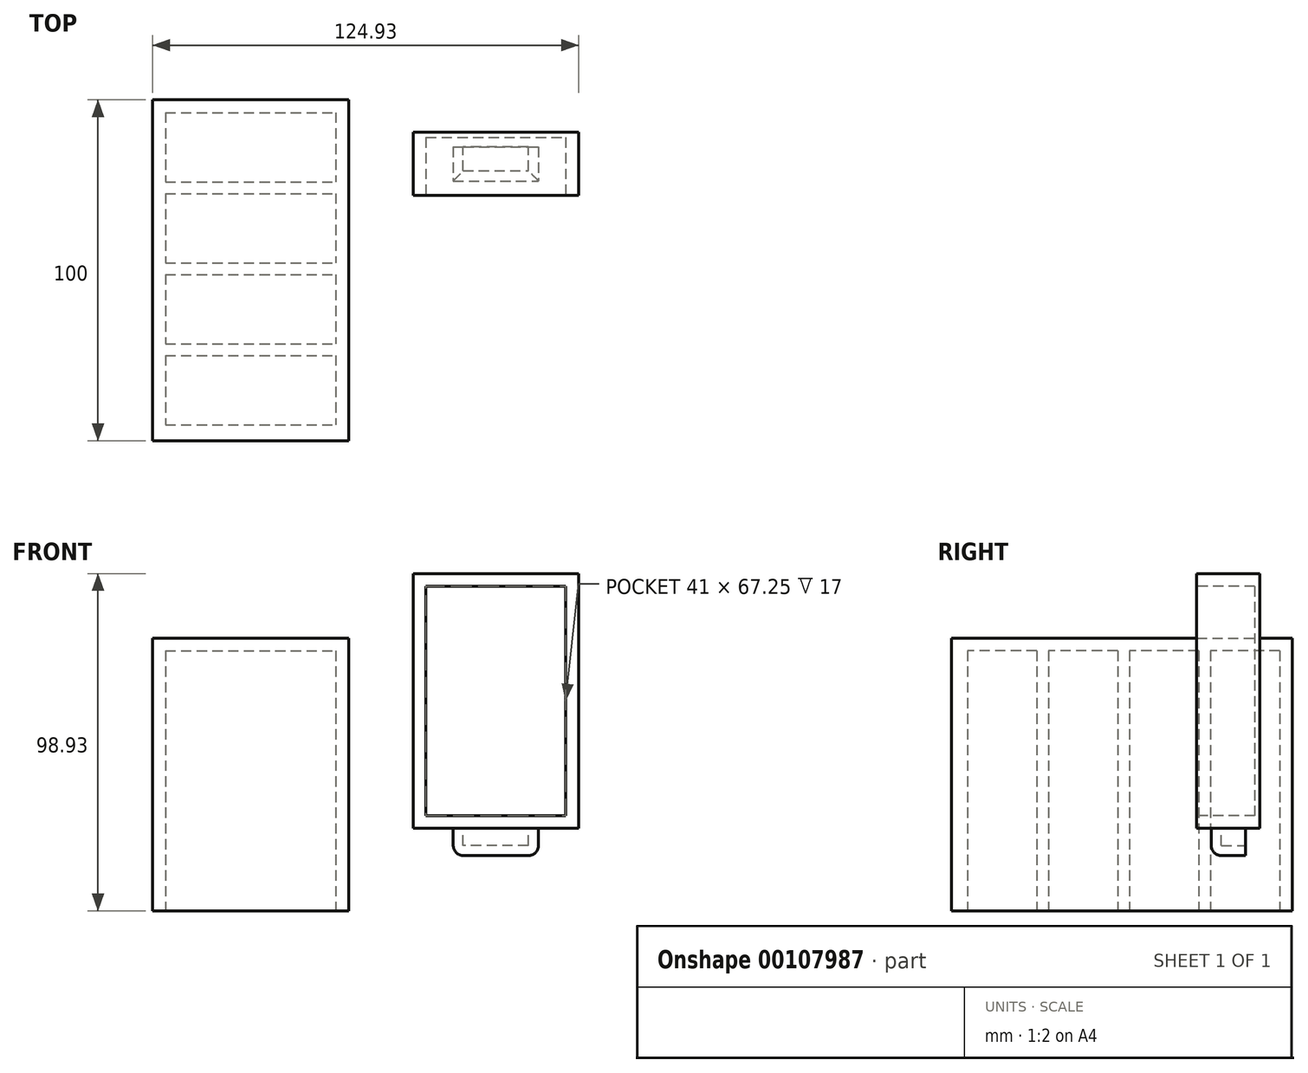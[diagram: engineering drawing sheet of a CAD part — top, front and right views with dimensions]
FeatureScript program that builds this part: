
annotation { "Feature Type Name" : "Feature", "Feature Type Description" : "" }
export const myFeature = defineFeature(function(context is Context, id is Id, definition is map)
    precondition{}
    {
        {
            var Q0;
            Q0=qCreatedBy(makeId("Front.planeOp"),FACE);
            var sketch = newSketch(context, id + "F0", { "sketchPlane" : qUnion([Q0])});
            skLineSegment(sketch, "E0.bottom", {"start": v(-28.56, 55.82) * mm, "end": v(28.94, 55.82) * mm});
            skLineSegment(sketch, "E0.top", {"start": v(-28.56, -24.18) * mm, "end": v(28.94, -24.18) * mm});
            skLineSegment(sketch, "E0.left", {"start": v(-28.56, 55.82) * mm, "end": v(-28.56, -24.18) * mm});
            skLineSegment(sketch, "E0.right", {"start": v(28.94, 55.82) * mm, "end": v(28.94, -24.18) * mm});
            skSolve(sketch);
        }
        {
            var Q0;
            Q0=makeQuery(id+"F0.imprint","IMPRINT",FACE,{"disambiguationData":[TD([[makeQuery(id+"F0.imprint","IMPRINT",EDGE,{"derivedFrom":sQuery(id+"F0.wireOp",EDGE,"E0.bottom")}),-1.0]])]});
            extrude(context, id + "F1", {"entities" : qUnion([Q0]), "depth" : 100 * mm});
        }
        {
            var Q0;
            Q0=makeQuery(id+"F1.opExtrude","SWEPT_FACE",FACE,{"disambiguationData":[OSD([sQuery(id+"F0.wireOp",EDGE,"E0.top")])]});
            var sketch = newSketch(context, id + "F2", { "sketchPlane" : qUnion([Q0])});
            skLineSegment(sketch, "E1.bottom", {"start": v(-24.81, 3.75) * mm, "end": v(25.19, 3.75) * mm});
            skLineSegment(sketch, "E1.top", {"start": v(-24.81, 24.06) * mm, "end": v(25.19, 24.06) * mm});
            skLineSegment(sketch, "E1.left", {"start": v(-24.81, 3.75) * mm, "end": v(-24.81, 24.06) * mm});
            skLineSegment(sketch, "E1.right", {"start": v(25.19, 3.75) * mm, "end": v(25.19, 24.06) * mm});
            skLineSegment(sketch, "E2.0.1.0", {"start": v(-24.81, 47.81) * mm, "end": v(25.19, 47.81) * mm});
            skLineSegment(sketch, "E2.0.1.1", {"start": v(25.19, 27.5) * mm, "end": v(25.19, 47.81) * mm});
            skLineSegment(sketch, "E2.0.1.2", {"start": v(-24.81, 27.5) * mm, "end": v(25.19, 27.5) * mm});
            skLineSegment(sketch, "E2.0.1.3", {"start": v(-24.81, 27.5) * mm, "end": v(-24.81, 47.81) * mm});
            skLineSegment(sketch, "E2.0.2.0", {"start": v(-24.81, 71.56) * mm, "end": v(25.19, 71.56) * mm});
            skLineSegment(sketch, "E2.0.2.1", {"start": v(25.19, 51.25) * mm, "end": v(25.19, 71.56) * mm});
            skLineSegment(sketch, "E2.0.2.2", {"start": v(-24.81, 51.25) * mm, "end": v(25.19, 51.25) * mm});
            skLineSegment(sketch, "E2.0.2.3", {"start": v(-24.81, 51.25) * mm, "end": v(-24.81, 71.56) * mm});
            skLineSegment(sketch, "E2.0.3.0", {"start": v(-24.81, 95.31) * mm, "end": v(25.19, 95.31) * mm});
            skLineSegment(sketch, "E2.0.3.1", {"start": v(25.19, 75) * mm, "end": v(25.19, 95.31) * mm});
            skLineSegment(sketch, "E2.0.3.2", {"start": v(-24.81, 75) * mm, "end": v(25.19, 75) * mm});
            skLineSegment(sketch, "E2.0.3.3", {"start": v(-24.81, 75) * mm, "end": v(-24.81, 95.31) * mm});
            skLineSegment(sketch, "E2.2.1.3", {"start": v(25.19, 27.5) * mm, "end": v(25.19, 47.81) * mm});
            skLineSegment(sketch, "E2.2.2.3", {"start": v(25.19, 51.25) * mm, "end": v(25.19, 71.56) * mm});
            skLineSegment(sketch, "E2.2.3.3", {"start": v(25.19, 75) * mm, "end": v(25.19, 95.31) * mm});
            skLineSegment(sketch, "E2.direction1", {"start": v(-24.81, 24.06) * mm, "end": v(0.19, 24.06) * mm, "construction": true});
            skLineSegment(sketch, "E2.direction2", {"start": v(-24.81, 24.06) * mm, "end": v(-24.81, 47.81) * mm, "construction": true});
            skSolve(sketch);
        }
        {
            var Q0;
            Q0 = qSketchRegion(id + "F2", true);
            extrude(context, id + "F3", {"entities" : qUnion([Q0]), "operationType" : NewBodyOperationType.REMOVE, "oppositeDirection" : true, "depth" : 76.25 * mm});
        }
        {
            var Q0;
            Q0=qCreatedBy(makeId("Top.planeOp"),FACE);
            var sketch = newSketch(context, id + "F4", { "sketchPlane" : qUnion([Q0])});
            skLineSegment(sketch, "E3.bottom", {"start": v(47.87, -28.06) * mm, "end": v(96.37, -28.06) * mm});
            skLineSegment(sketch, "E3.top", {"start": v(47.87, -9.56) * mm, "end": v(96.37, -9.56) * mm});
            skLineSegment(sketch, "E3.left", {"start": v(47.87, -28.06) * mm, "end": v(47.87, -9.56) * mm});
            skLineSegment(sketch, "E3.right", {"start": v(96.37, -28.06) * mm, "end": v(96.37, -9.56) * mm});
            skSolve(sketch);
        }
        {
            var Q0;
            Q0 = qSketchRegion(id + "F4", true);
            extrude(context, id + "F5", {"entities" : qUnion([Q0]), "depth" : 74.75 * mm});
        }
        {
            var Q0;
            Q0=makeQuery(id+"F5.opExtrude","CAP_FACE",FACE,{"disambiguationData":[OSD([sQuery(id+"F4.wireOp",EDGE,"E3.bottom"),sQuery(id+"F4.wireOp",EDGE,"E3.top"),sQuery(id+"F4.wireOp",EDGE,"E3.left"),sQuery(id+"F4.wireOp",EDGE,"E3.right")])],"isStart":true});
            var sketch = newSketch(context, id + "F6", { "sketchPlane" : qUnion([Q0])});
            skLineSegment(sketch, "E4", {"start": v(72.12, 28.06) * mm, "end": v(72.12, 9.56) * mm});
            skPoint(sketch, "E5", {"position": v(72.12, 18.81) * mm});
            skLineSegment(sketch, "E6", {"start": v(72.12, 18.81) * mm, "end": v(47.87, 18.81) * mm});
            skLineSegment(sketch, "E7", {"start": v(72.12, 18.81) * mm, "end": v(96.37, 18.81) * mm});
            skLineSegment(sketch, "E8.bottom", {"start": v(59.62, 13.81) * mm, "end": v(84.62, 13.81) * mm});
            skLineSegment(sketch, "E8.top", {"start": v(59.62, 23.81) * mm, "end": v(84.62, 23.81) * mm});
            skLineSegment(sketch, "E8.left", {"start": v(59.62, 13.81) * mm, "end": v(59.62, 23.81) * mm});
            skLineSegment(sketch, "E8.right", {"start": v(84.62, 13.81) * mm, "end": v(84.62, 23.81) * mm});
            skSolve(sketch);
        }
        {
            var Q0;
            Q0 = qSketchRegion(id + "F6", true);
            extrude(context, id + "F7", {"entities" : qUnion([Q0]), "operationType" : NewBodyOperationType.ADD, "depth" : 8 * mm});
        }
        {
            var Q0;
            Q0=makeQuery(id+"F7.opExtrude","CAP_EDGE",EDGE,{"disambiguationData":[OSD([sQuery(id+"F6.wireOp",EDGE,"E8.top")])],"isStart":false});
            var Q1;
            Q1=makeQuery(id+"F7.opExtrude","CAP_EDGE",EDGE,{"disambiguationData":[OSD([sQuery(id+"F6.wireOp",EDGE,"E8.left")])],"isStart":false});
            var Q2;
            Q2=makeQuery(id+"F7.opExtrude","CAP_EDGE",EDGE,{"disambiguationData":[OSD([sQuery(id+"F6.wireOp",EDGE,"E8.right")])],"isStart":false});
            fillet(context, id + "F8", {"entities" : qUnion([Q0, Q1, Q2]), "radius" : 3 * mm, "tangentPropagation" : true, "allowEdgeOverflow" : false});
        }
        {
            var Q0;
            Q0=makeQuery(id+"F7.opExtrude","SWEPT_FACE",FACE,{"disambiguationData":[OSD([sQuery(id+"F6.wireOp",EDGE,"E8.bottom")])]});
            var sketch = newSketch(context, id + "F9", { "sketchPlane" : qUnion([Q0])});
            skLineSegment(sketch, "E9.bottom", {"start": v(-81.62, -5) * mm, "end": v(-62.5, -5) * mm});
            skLineSegment(sketch, "E9.top", {"start": v(-81.62, 0) * mm, "end": v(-62.5, 0) * mm});
            skLineSegment(sketch, "E9.left", {"start": v(-81.62, -5) * mm, "end": v(-81.62, 0) * mm});
            skLineSegment(sketch, "E9.right", {"start": v(-62.5, -5) * mm, "end": v(-62.5, 0) * mm});
            skSolve(sketch);
        }
        {
            var Q0;
            Q0 = qSketchRegion(id + "F9", true);
            extrude(context, id + "F10", {"entities" : qUnion([Q0]), "operationType" : NewBodyOperationType.REMOVE, "oppositeDirection" : true, "depth" : 7 * mm});
        }
        {
            var Q0;
            Q0=makeQuery(id+"F5.opExtrude","SWEPT_FACE",FACE,{"disambiguationData":[OSD([sQuery(id+"F4.wireOp",EDGE,"E3.bottom")])]});
            var sketch = newSketch(context, id + "F11", { "sketchPlane" : qUnion([Q0])});
            skLineSegment(sketch, "E10.bottom", {"start": v(51.62, 71) * mm, "end": v(92.62, 71) * mm});
            skLineSegment(sketch, "E10.top", {"start": v(51.62, 3.75) * mm, "end": v(92.62, 3.75) * mm});
            skLineSegment(sketch, "E10.left", {"start": v(51.62, 71) * mm, "end": v(51.62, 3.75) * mm});
            skLineSegment(sketch, "E10.right", {"start": v(92.62, 71) * mm, "end": v(92.62, 3.75) * mm});
            skSolve(sketch);
        }
        {
            var Q0;
            Q0 = qSketchRegion(id + "F11", true);
            extrude(context, id + "F12", {"entities" : qUnion([Q0]), "operationType" : NewBodyOperationType.REMOVE, "oppositeDirection" : true, "depth" : 17 * mm});
        }
    });
